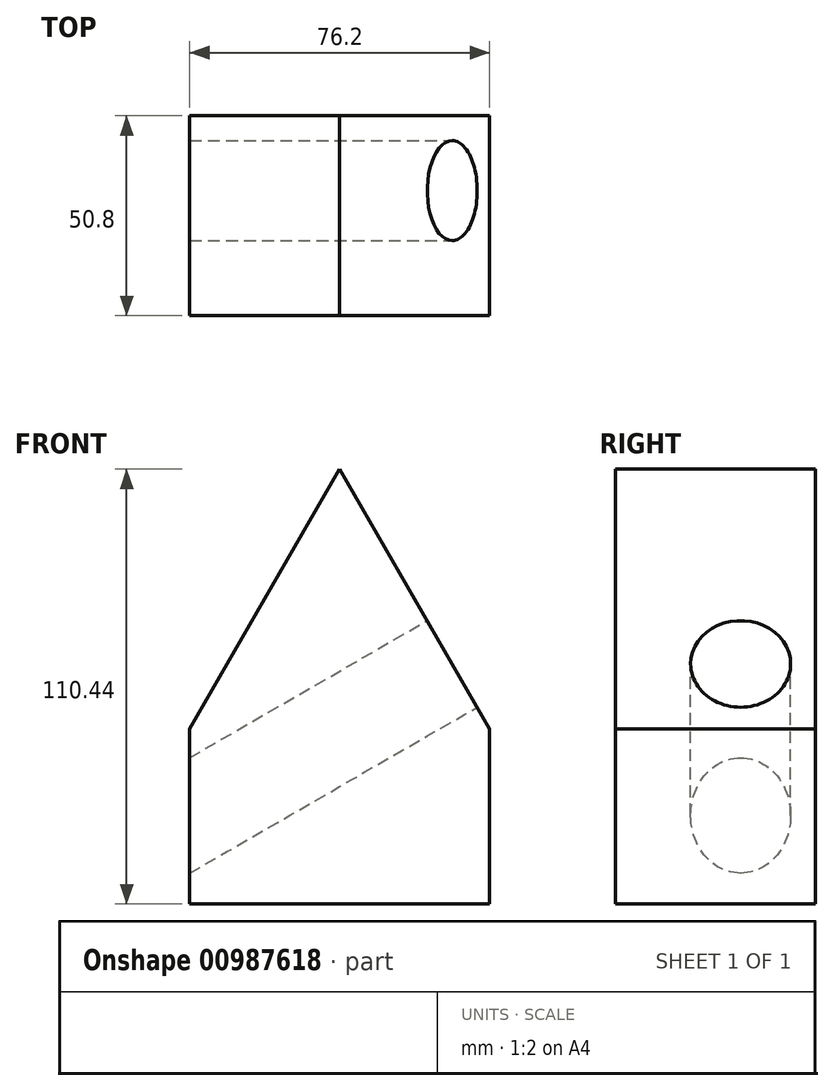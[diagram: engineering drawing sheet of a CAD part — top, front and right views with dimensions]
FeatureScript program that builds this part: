
annotation { "Feature Type Name" : "Feature", "Feature Type Description" : "" }
export const myFeature = defineFeature(function(context is Context, id is Id, definition is map)
    precondition{}
    {
        {
            var Q0;
            Q0=qCreatedBy(makeId("Front.planeOp"),FACE);
            var sketch = newSketch(context, id + "F0", { "sketchPlane" : qUnion([Q0])});
            skLineSegment(sketch, "E0.bottom", {"start": v(0, 0) * mm, "end": v(76.2, 0) * mm});
            skLineSegment(sketch, "E0.top", {"start": v(0, 44.45) * mm, "end": v(76.2, 44.45) * mm});
            skLineSegment(sketch, "E0.left", {"start": v(0, 0) * mm, "end": v(0, 44.45) * mm});
            skLineSegment(sketch, "E0.right", {"start": v(76.2, 0) * mm, "end": v(76.2, 44.45) * mm});
            skLineSegment(sketch, "E1", {"start": v(0, 44.45) * mm, "end": v(38.1, 110.44) * mm});
            skLineSegment(sketch, "E2", {"start": v(38.1, 110.44) * mm, "end": v(76.2, 44.45) * mm});
            skSolve(sketch);
        }
        {
            var Q0;
            Q0 = qSketchRegion(id + "F0", true);
            extrude(context, id + "F1", {"entities" : qUnion([Q0]), "depth" : 50.8 * mm, "offsetDistance" : 25.4 * mm});
        }
        {
            var Q0;
            Q0=makeQuery(id+"F1.opExtrude","SWEPT_FACE",FACE,{"disambiguationData":[OSD([sQuery(id+"F0.wireOp",EDGE,"E2")])]});
            var sketch = newSketch(context, id + "F2", { "sketchPlane" : qUnion([Q0])});
            skCircle(sketch, "E3", {"center": v(-19.05, 19.44) * mm, "radius": 12.7 * mm});
            skSolve(sketch);
        }
        {
            var Q0;
            Q0 = qSketchRegion(id + "F2", true);
            extrude(context, id + "F3", {"entities" : qUnion([Q0]), "operationType" : NewBodyOperationType.REMOVE, "endBound" : BoundingType.THROUGH_ALL, "oppositeDirection" : true, "depth" : 127 * mm, "offsetDistance" : 25.4 * mm});
        }
    });
